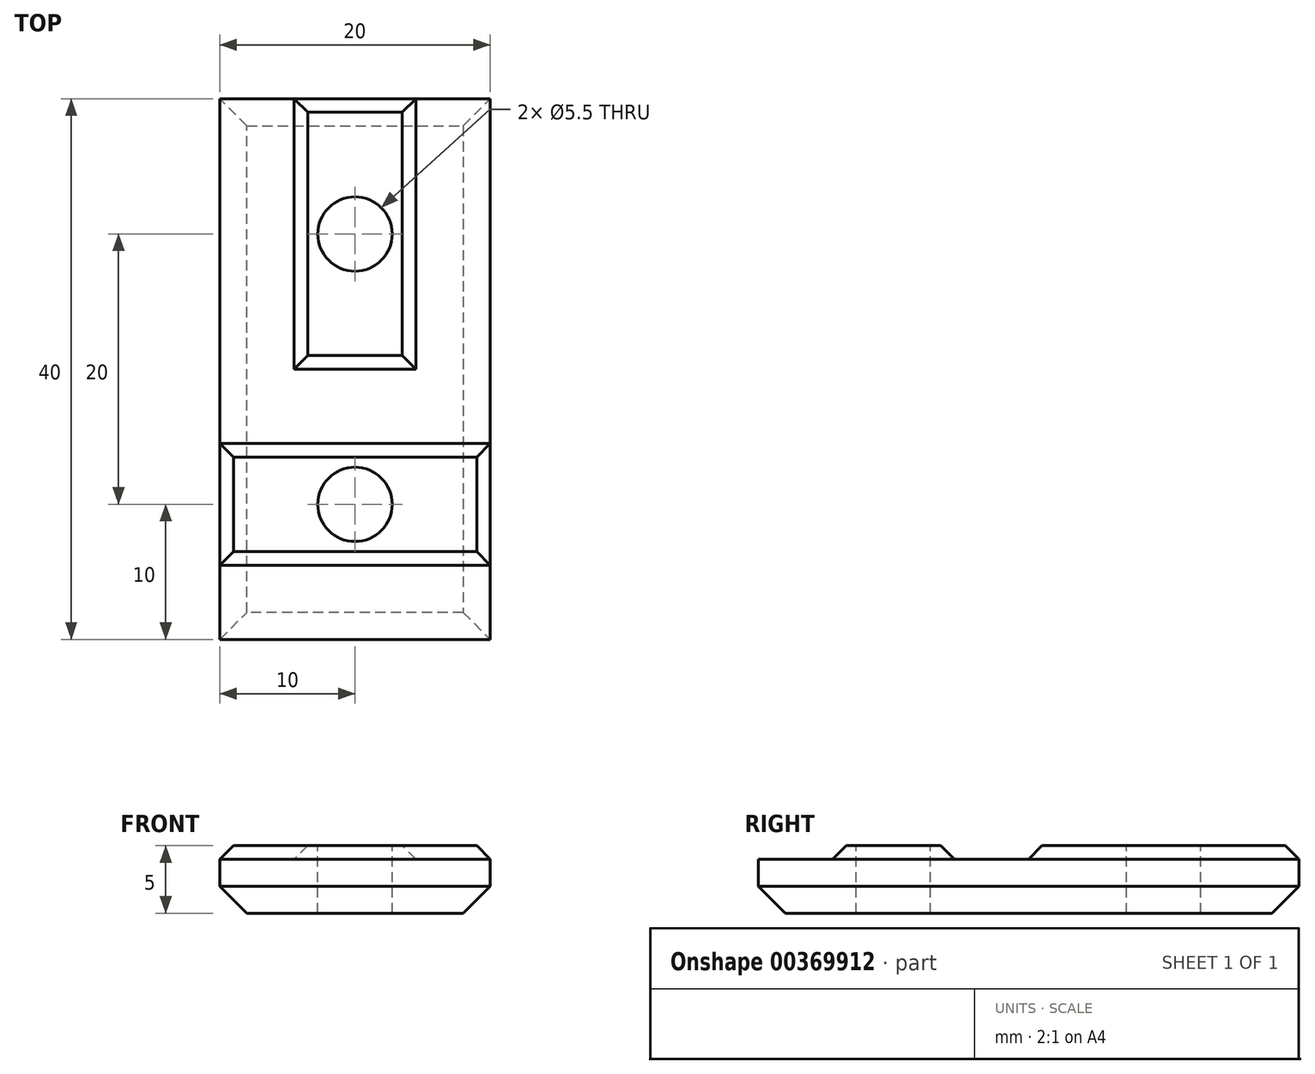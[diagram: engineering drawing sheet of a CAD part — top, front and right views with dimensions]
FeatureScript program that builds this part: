
annotation { "Feature Type Name" : "Feature", "Feature Type Description" : "" }
export const myFeature = defineFeature(function(context is Context, id is Id, definition is map)
    precondition{}
    {
        {
            var Q0;
            Q0=qCreatedBy(makeId("Top.planeOp"),FACE);
            var sketch = newSketch(context, id + "F0", { "sketchPlane" : qUnion([Q0])});
            skLineSegment(sketch, "E0.bottom", {"start": v(0, 0) * mm, "end": v(20, 0) * mm});
            skLineSegment(sketch, "E0.top", {"start": v(0, 40) * mm, "end": v(20, 40) * mm});
            skLineSegment(sketch, "E0.left", {"start": v(0, 0) * mm, "end": v(0, 40) * mm});
            skLineSegment(sketch, "E0.right", {"start": v(20, 0) * mm, "end": v(20, 40) * mm});
            skPoint(sketch, "E1.centerSnap0", {"position": v(10, 40) * mm});
            skSolve(sketch);
        }
        {
            var Q0;
            Q0 = qSketchRegion(id + "F0", true);
            extrude(context, id + "F1", {"entities" : qUnion([Q0]), "depth" : 4 * mm});
        }
        {
            var Q0;
            Q0=makeQuery(id+"F1.opExtrude","CAP_FACE",FACE,{"disambiguationData":[OSD([sQuery(id+"F0.wireOp",EDGE,"E0.bottom"),sQuery(id+"F0.wireOp",EDGE,"E0.top"),sQuery(id+"F0.wireOp",EDGE,"E0.left"),sQuery(id+"F0.wireOp",EDGE,"E0.right")])],"isStart":false});
            var sketch = newSketch(context, id + "F2", { "sketchPlane" : qUnion([Q0])});
            skLineSegment(sketch, "E2.bottom", {"start": v(5.5, 40) * mm, "end": v(14.5, 40) * mm});
            skLineSegment(sketch, "E2.top", {"start": v(5.5, 20) * mm, "end": v(14.5, 20) * mm});
            skLineSegment(sketch, "E2.left", {"start": v(5.5, 40) * mm, "end": v(5.5, 20) * mm});
            skLineSegment(sketch, "E2.right", {"start": v(14.5, 40) * mm, "end": v(14.5, 20) * mm});
            skLineSegment(sketch, "E3.bottom", {"start": v(0, 14.5) * mm, "end": v(20, 14.5) * mm});
            skLineSegment(sketch, "E3.top", {"start": v(0, 5.5) * mm, "end": v(20, 5.5) * mm});
            skLineSegment(sketch, "E3.left", {"start": v(0, 14.5) * mm, "end": v(0, 5.5) * mm});
            skLineSegment(sketch, "E3.right", {"start": v(20, 14.5) * mm, "end": v(20, 5.5) * mm});
            skSolve(sketch);
        }
        {
            var Q0;
            Q0 = qSketchRegion(id + "F2", true);
            extrude(context, id + "F3", {"entities" : qUnion([Q0]), "operationType" : NewBodyOperationType.ADD, "depth" : 1 * mm});
        }
        {
            var Q0;
            Q0=makeQuery(id+"F3.opExtrude","CAP_FACE",FACE,{"disambiguationData":[OSD([sQuery(id+"F2.wireOp",EDGE,"E2.bottom"),sQuery(id+"F2.wireOp",EDGE,"E2.top"),sQuery(id+"F2.wireOp",EDGE,"E2.left"),sQuery(id+"F2.wireOp",EDGE,"E2.right")])],"isStart":false});
            var Q1;
            Q1=makeQuery(id+"F3.opExtrude","CAP_FACE",FACE,{"disambiguationData":[OSD([sQuery(id+"F2.wireOp",EDGE,"E3.bottom"),sQuery(id+"F2.wireOp",EDGE,"E3.top"),sQuery(id+"F2.wireOp",EDGE,"E3.left"),sQuery(id+"F2.wireOp",EDGE,"E3.right")])],"isStart":false});
            chamfer(context, id + "F4", {"entities" : qUnion([Q0, Q1]), "width" : 1 * mm, "tangentPropagation" : true});
        }
        {
            var Q0;
            Q0=makeQuery(id+"F3.opExtrude","CAP_FACE",FACE,{"disambiguationData":[OSD([sQuery(id+"F2.wireOp",EDGE,"E2.bottom"),sQuery(id+"F2.wireOp",EDGE,"E2.top"),sQuery(id+"F2.wireOp",EDGE,"E2.left"),sQuery(id+"F2.wireOp",EDGE,"E2.right")])],"isStart":false});
            var sketch = newSketch(context, id + "F5", { "sketchPlane" : qUnion([Q0])});
            skCircle(sketch, "E4", {"center": v(10, 30) * mm, "radius": 2.75 * mm});
            skPoint(sketch, "E4.centerSnap0", {"position": v(10, 39) * mm});
            skPoint(sketch, "E4.centerSnap1", {"position": v(13.5, 30) * mm});
            skLineSegment(sketch, "E5.0", {"start": v(1, 13.5) * mm, "end": v(1, 6.5) * mm, "construction": true});
            skCircle(sketch, "E6", {"center": v(10, 10) * mm, "radius": 2.75 * mm});
            skPoint(sketch, "E6.centerSnap0", {"position": v(10, 21) * mm});
            skPoint(sketch, "E6.centerSnap1", {"position": v(1, 10) * mm});
            skSolve(sketch);
        }
        {
            var Q0;
            Q0 = qSketchRegion(id + "F5", true);
            extrude(context, id + "F6", {"entities" : qUnion([Q0]), "operationType" : NewBodyOperationType.REMOVE, "endBound" : BoundingType.THROUGH_ALL, "oppositeDirection" : true, "depth" : 25 * mm});
        }
        {
            var Q0;
            Q0=makeQuery(id+"F1.opExtrude","CAP_EDGE",EDGE,{"disambiguationData":[OSD([sQuery(id+"F0.wireOp",EDGE,"E0.left")])],"isStart":true});
            var Q1;
            Q1=makeQuery(id+"F1.opExtrude","CAP_EDGE",EDGE,{"disambiguationData":[OSD([sQuery(id+"F0.wireOp",EDGE,"E0.bottom")])],"isStart":true});
            var Q2;
            Q2=makeQuery(id+"F1.opExtrude","CAP_EDGE",EDGE,{"disambiguationData":[OSD([sQuery(id+"F0.wireOp",EDGE,"E0.right")])],"isStart":true});
            var Q3;
            Q3=makeQuery(id+"F1.opExtrude","CAP_EDGE",EDGE,{"disambiguationData":[OSD([sQuery(id+"F0.wireOp",EDGE,"E0.top")])],"isStart":true});
            chamfer(context, id + "F7", {"entities" : qUnion([Q0, Q1, Q2, Q3]), "width" : 2 * mm, "tangentPropagation" : true});
        }
    });
